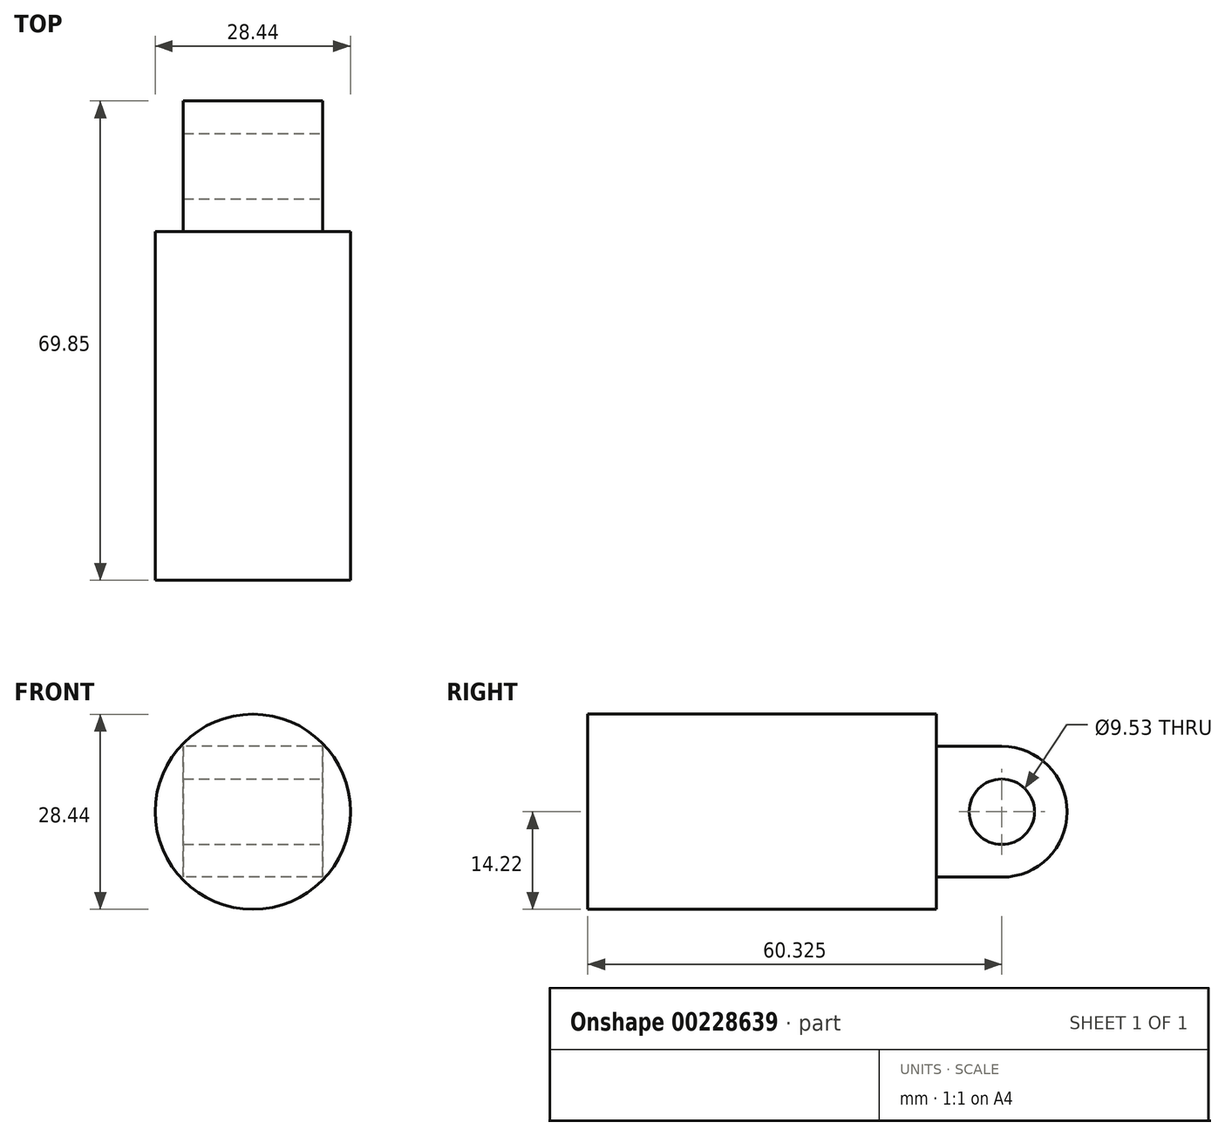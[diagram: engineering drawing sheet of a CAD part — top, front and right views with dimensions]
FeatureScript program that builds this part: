
annotation { "Feature Type Name" : "Feature", "Feature Type Description" : "" }
export const myFeature = defineFeature(function(context is Context, id is Id, definition is map)
    precondition{}
    {
        {
            var Q0;
            Q0=qCreatedBy(makeId("Front.planeOp"),FACE);
            var sketch = newSketch(context, id + "F0", { "sketchPlane" : qUnion([Q0])});
            skCircle(sketch, "E0", {"center": v(0, 0) * mm, "radius": 14.22 * mm});
            skSolve(sketch);
        }
        {
            var Q0;
            Q0 = qSketchRegion(id + "F0", true);
            extrude(context, id + "F1", {"entities" : qUnion([Q0]), "depth" : 50.8 * mm, "offsetDistance" : 25.4 * mm});
        }
        {
            var Q0;
            Q0=qCreatedBy(makeId("Right.planeOp"),FACE);
            var sketch = newSketch(context, id + "F2", { "sketchPlane" : qUnion([Q0])});
            skLineSegment(sketch, "E1.bottom", {"start": v(19.05, 9.53) * mm, "end": v(0, 9.53) * mm});
            skLineSegment(sketch, "E1.top", {"start": v(19.05, -9.52) * mm, "end": v(0, -9.53) * mm});
            skLineSegment(sketch, "E1.left", {"start": v(19.05, 9.53) * mm, "end": v(19.05, -9.52) * mm});
            skLineSegment(sketch, "E1.right", {"start": v(0, 9.53) * mm, "end": v(0, -9.53) * mm});
            skSolve(sketch);
        }
        {
            var Q0;
            Q0 = qSketchRegion(id + "F2", true);
            extrude(context, id + "F3", {"entities" : qUnion([Q0]), "operationType" : NewBodyOperationType.ADD, "endBound" : BoundingType.SYMMETRIC, "depth" : 20.32 * mm, "offsetDistance" : 25.4 * mm});
        }
        {
            var Q0;
            Q0=makeQuery(id+"F3.opExtrude","CAP_FACE",FACE,{"disambiguationData":[OSD([sQuery(id+"F2.wireOp",EDGE,"E1.bottom"),sQuery(id+"F2.wireOp",EDGE,"E1.top"),sQuery(id+"F2.wireOp",EDGE,"E1.left"),sQuery(id+"F2.wireOp",EDGE,"E1.right")])],"isStart":false});
            var sketch = newSketch(context, id + "F4", { "sketchPlane" : qUnion([Q0])});
            skCircle(sketch, "E2", {"center": v(9.53, 0) * mm, "radius": 4.76 * mm});
            skSolve(sketch);
        }
        {
            var Q0;
            Q0 = qSketchRegion(id + "F4", true);
            extrude(context, id + "F5", {"entities" : qUnion([Q0]), "operationType" : NewBodyOperationType.REMOVE, "oppositeDirection" : true, "depth" : 25.4 * mm, "offsetDistance" : 25.4 * mm});
        }
        {
            var Q0;
            Q0=makeQuery(id+"F3.opExtrude","SWEPT_EDGE",EDGE,{"disambiguationData":[OSD([sQuery(id+"F2.wireOp",EDGE,"E1.bottom"),sQuery(id+"F2.wireOp",EDGE,"E1.left")])]});
            var Q1;
            Q1=makeQuery(id+"F3.opExtrude","SWEPT_EDGE",EDGE,{"disambiguationData":[OSD([sQuery(id+"F2.wireOp",EDGE,"E1.top"),sQuery(id+"F2.wireOp",EDGE,"E1.left")])]});
            fillet(context, id + "F6", {"entities" : qUnion([Q0, Q1]), "radius" : 9.52 * mm, "tangentPropagation" : true, "allowEdgeOverflow" : false});
        }
    });
